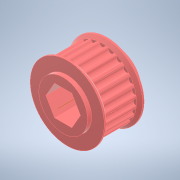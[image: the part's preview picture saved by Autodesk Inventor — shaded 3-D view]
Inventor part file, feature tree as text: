
AUTODESK INVENTOR PART (.ipt)
format: ipt  version: 2022.3 (Build 263350000, 350)  size: 331,264 bytes
history: native  units: in
note: dims shown in document units (in); Inventor stores cm internally (conversion verified against a paired STEP export)
features: extrude x8, sketch x7, mirror x2, chamfer x2, other x1, fillet x1, pattern_circular x1, projected_geometry x1
ambient origin geometry x8: Origin, YZ Plane, XZ Plane, XY Plane, X Axis, Y Axis, Z Axis, Center Point
bodies: Solid1 (feature_tree)
feature tree (23):
  other  "Hex Bore"
  extrude  "HTD Base"  Depth=0.3937in TaperAngle=0.0deg
  extrude  "HTD Flange"  Depth=0.0591in
  mirror  "HTD Flanges"
  chamfer  "HTD Flange Chamfer"  Distance=0.0787in Angle=45.0deg
  extrude  "GT2 Base"  TaperAngle=0.0deg  [1 undecoded]
  extrude  "GT2 Base Tooth"  TaperAngle=0.0deg  [1 undecoded]
  fillet  "GT2 Base Tooth pt. 2"  Radius=0.8723in
  pattern_circular  "GT2 Teeth"  [2 undecoded]
  extrude  "GT2 Flange"  Depth=0.5638in
  mirror  "GT2 Flanges"
  chamfer  "GT2 Flange Chamfer"  Distance=0.0075in
  extrude  "Circle Bore"  TaperAngle=0.0deg  [1 undecoded]
  sketch  "Sketch9"  dims[d25=0.3937in d26=0.0in d27=0.0727in d28=0.0075in d29=0.0in d30=0.0in d31=0.0118in d32=9.4488in d33=360.0deg d35=0.0394in d36=0.0591in d37=0.0in d38=0.0394in d39=0.0787in d40=45.0deg d41=0.625in d42=0.125in d43=0.0in d44=0.5638in d45=0.0in]
  extrude  "Extrusion10"  Depth=0.0118in
  extrude  "Extrusion9"  Depth=0.5638in
  sketch  "Sketch1"  dims[d0=1.4588in d1=0.3937in d2=0.0in]
  sketch  "Sketch4"  dims[d12=0.0394in d13=0.0591in]
  sketch  "Sketch5"  dims[d14=0.0in]
  sketch  "Sketch6"  dims[d15=0.0394in d16=0.0787in d17=45.0deg]
  sketch  "Sketch7"  dims[d18=0.385in d19=0.0in d20=0.0in]
  sketch  "Sketch8"  dims[d21=0.385in d22=0.0in d23=0.0in d24=0.8723in]
  projected_geometry  "Projected Loop1"
note: 5 required parameter values undecoded (feature->parameter linkage not recoverable at this tier; creation-order binding heuristic only, values carry confidence <= 0.55)
